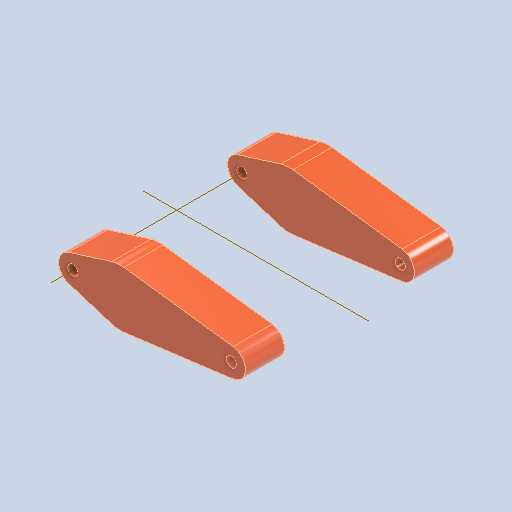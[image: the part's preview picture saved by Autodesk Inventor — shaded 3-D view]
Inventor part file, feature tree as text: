
AUTODESK INVENTOR PART (.ipt)
format: ipt  version: 2025 (Build 290162000, 162)  size: 174,592 bytes
history: native  units: mm
features: sketch x6, hole x4, other x2, extrude x2, plane x1, mirror x1
ambient origin geometry x8: Origin, YZ Plane, XZ Plane, XY Plane, X Axis, Y Axis, Z Axis, Center Point
bodies: Body1 (feature_tree)
feature tree (16):
  parser-record x1  (decoder bookkeeping rows leaked as tree rows — omitted from the tree; the rows remain in map.json)
  other  "實體1"
  plane  "工作平面1"
  extrude  "擠出1"  Depth=275.0mm
  extrude  "擠出2"  Depth=419.3047mm
  hole  "孔1"  [1 undecoded]
  hole  "孔2"  [1 undecoded]
  hole  "孔4"  [1 undecoded]
  hole  "孔5"  [1 undecoded]
  mirror  "鏡射1"
  sketch  "草圖1"
  sketch  "草圖2"
  sketch  "草圖3"
  sketch  "草圖4"
  sketch  "草圖6"
  sketch  "草圖7"
note: 4 required parameter values undecoded (feature->parameter linkage not recoverable at this tier; creation-order binding heuristic only, values carry confidence <= 0.55)
note: 1 file-system path scrubbed to <path> (originals preserved in map.json)
